# Revit family: SUPERBRILLOSA DIFUSA 2216_S242300U.1_N.1
name_source: partatom
category: Luminarias
units: mm (PartAtom-declared; Revit-internal decimal feet)

## family parameters
Compartido = No
Corte con vacíos al cargar = No
Cota de conector redondo = Diámetro de uso
Origen de luz = Sí
Punto de cálculo de habitación = No
Se basa en plano de trabajo = Sí
Siempre vertical = No
Tipo de pieza = Normal

## types (2) — shared parameters
Cambio de temperatura de color de luz atenuada = <Ninguno>
Comentarios de vataje = 24
Fabricante = BRILLANT
Filtro de color = 16777215
Longitud de línea de emisión = 600 mm
Marca = BRILLANT
Tamaño de símbolo de origen de luz = 610 mm
zero-valued in all types: Elevación por defecto

## per-type parameters (varying)
| type | Descripción | Modelo |
| SUPERBRILLOSA DIFUSA 2216_S242300U.1 | TIRA LUMINOSA MONOCROMATICADE PCB BLANCO CON RECUBRIMIENTO DE PLASTICO CON UNA POTENCIA DE 15W/M, USO PARA EXTERIORES IP66, IRC 90,  TEMPERATURA EN BLANCO CALIDO 3000K, 1245 LUMENES/M, PRESENTACION DE 5M, CORTE 2.5CM, ALIMENTADO A 24V, REQUIERE ACCESORIOS. | S242300U.1 |
| SUPERBRILLOSA DIFUSA 2216_S242300N.1 | TIRA LUMINOSA MONOCROMATICADE PCB BLANCO CON RECUBRIMIENTO DE PLASTICO CON UNA POTENCIA DE 15W/M, USO PARA EXTERIORES IP66, IRC 90,  TEMPERATURA EN BLANCO FRIO 4000K, 1350 LUMENES/M, PRESENTACION DE 5M, CORTE 2.5CM, ALIMENTADO A 24V, REQUIERE ACCESORIOS. | S242300N.1 |

## geometry (parser evidence)
native form markers: Blend x2
no freeform markers — native parametric forms only
